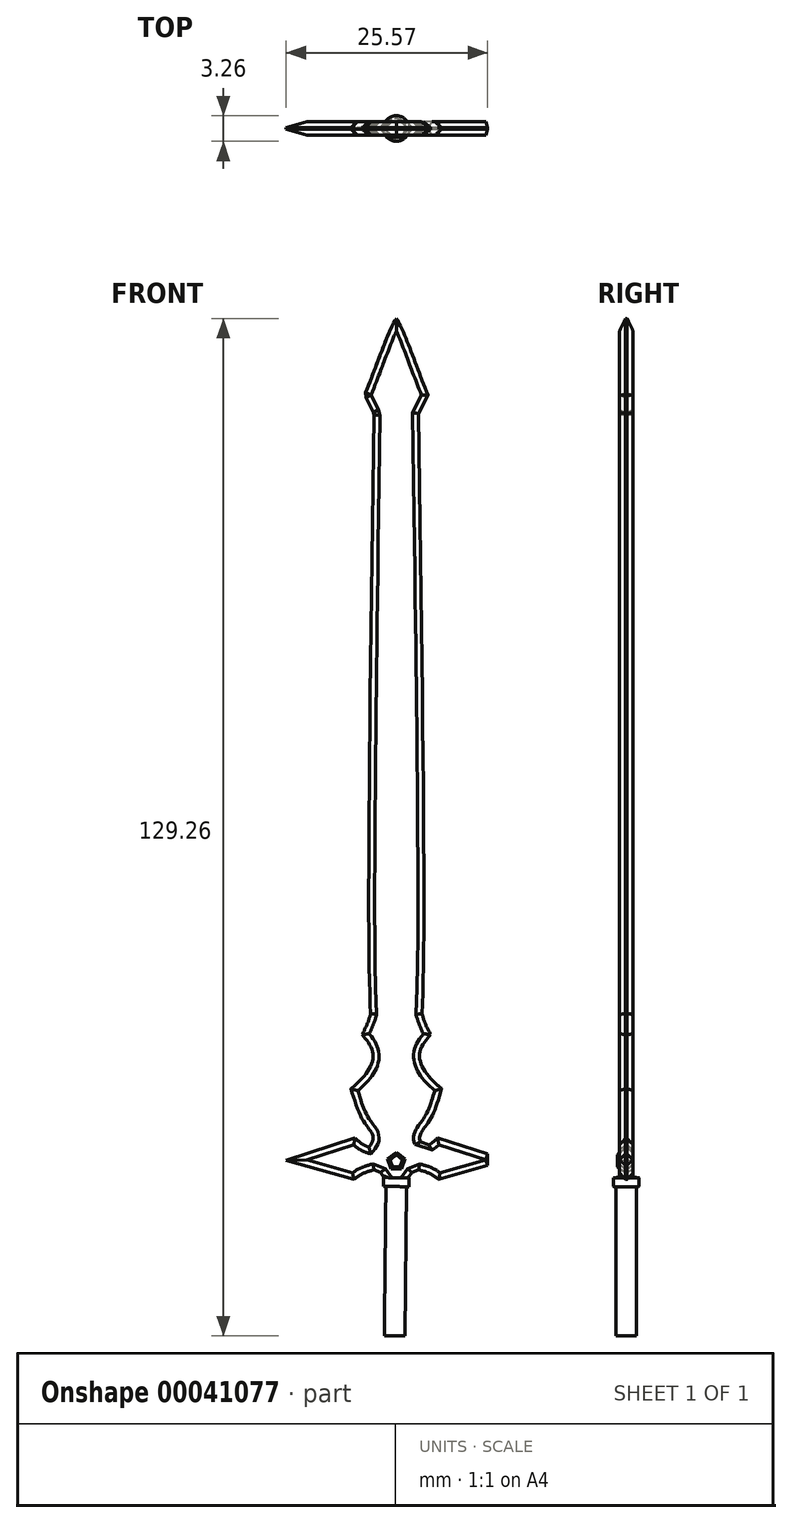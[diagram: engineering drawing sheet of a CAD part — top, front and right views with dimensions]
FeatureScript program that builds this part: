
annotation { "Feature Type Name" : "Feature", "Feature Type Description" : "" }
export const myFeature = defineFeature(function(context is Context, id is Id, definition is map)
    precondition{}
    {
        {
            var Q0;
            Q0=qCreatedBy(makeId("Front.planeOp"),FACE);
            var sketch = newSketch(context, id + "F0", { "sketchPlane" : qUnion([Q0])});
            skFitSpline(sketch, "E0", {"points": [v(5.64, -23.5) * mm, v(4.37, -24.78) * mm, v(3, -26.96) * mm, v(3.73, -29.6) * mm, v(7.73, -33.15) * mm], "startDerivative": vector(-6.28, -5.97) * mm, "endDerivative": vector(13.99, -10.4) * mm});
            skFitSpline(sketch, "E1", {"points": [v(6.28, -29.78) * mm, v(4.28, -35.6) * mm, v(3.1, -37.33) * mm, v(3.1, -38.51) * mm, v(5.19, -40.52) * mm], "startDerivative": vector(-5, -18.26) * mm, "endDerivative": vector(10.5, -8.04) * mm});
            skFitSpline(sketch, "E2", {"points": [v(6.17, -26.5) * mm, v(5.19, -25.87) * mm, v(3.46, -22.78) * mm, v(2.64, -18.05) * mm], "startDerivative": vector(-4.56, 2.08) * mm, "endDerivative": vector(-1.1, 11.4) * mm});
            skFitSpline(sketch, "E3", {"points": [v(3.1, -25.05) * mm, v(3.46, -15.5) * mm, v(2.8, 56.95) * mm], "startDerivative": vector(1.67, 27.47) * mm, "endDerivative": vector(-1.73, 121.84) * mm});
            skFitSpline(sketch, "E4", {"points": [v(1.28, 51.03) * mm, v(5.66, 59.65) * mm], "startDerivative": vector(4.37, 8.62) * mm, "endDerivative": vector(4.37, 8.62) * mm});
            skFitSpline(sketch, "E5", {"points": [v(-2.07, 68.66) * mm, v(0, 66.21) * mm, v(2.36, 60.7) * mm, v(5.42, 52.98) * mm], "startDerivative": vector(8.58, -8.47) * mm, "endDerivative": vector(7.87, -19.45) * mm});
            skFitSpline(sketch, "E6", {"points": [v(2.5, -39.2) * mm, v(3.96, -38.89) * mm, v(6, -37.16) * mm], "startDerivative": vector(3.37, 0.26) * mm, "endDerivative": vector(3.62, 3.67) * mm});
            skFitSpline(sketch, "E7", {"points": [v(4.55, -37.7) * mm, v(15.78, -41.3) * mm], "startDerivative": vector(11.23, -3.6) * mm, "endDerivative": vector(11.23, -3.6) * mm});
            skFitSpline(sketch, "E8", {"points": [v(4.69, -43.39) * mm, v(15.46, -40.3) * mm], "startDerivative": vector(10.78, 3.1) * mm, "endDerivative": vector(10.78, 3.1) * mm});
            skFitSpline(sketch, "E9", {"points": [v(6, -43.8) * mm, v(4.46, -42.53) * mm, v(1.68, -41.7) * mm], "startDerivative": vector(-3.02, 3.1) * mm, "endDerivative": vector(-5.54, 1.14) * mm});
            skFitSpline(sketch, "E10", {"points": [v(2.87, -41.07) * mm, v(0.87, -43.84) * mm], "startDerivative": vector(-2, -2.77) * mm, "endDerivative": vector(-2, -2.77) * mm});
            skFitSpline(sketch, "E11", {"points": [v(2.46, -42.98) * mm, v(-2.9, -42.92) * mm], "startDerivative": vector(-5.37, 0.06) * mm, "endDerivative": vector(-5.37, 0.06) * mm});
            skFitSpline(sketch, "E12.MirrorCS", {"points": [v(-6, -43.8) * mm, v(-4.46, -42.53) * mm, v(-1.68, -41.7) * mm], "startDerivative": vector(3.02, 3.1) * mm, "endDerivative": vector(5.54, 1.14) * mm});
            skFitSpline(sketch, "E13.MirrorCS", {"points": [v(-2.87, -41.07) * mm, v(-0.87, -43.84) * mm], "startDerivative": vector(2, -2.77) * mm, "endDerivative": vector(2, -2.77) * mm});
            skFitSpline(sketch, "E14.MirrorCS", {"points": [v(-2.5, -39.2) * mm, v(-3.96, -38.89) * mm, v(-6, -37.16) * mm], "startDerivative": vector(-3.37, 0.26) * mm, "endDerivative": vector(-3.62, 3.67) * mm});
            skFitSpline(sketch, "E15.MirrorCS", {"points": [v(-6.17, -26.5) * mm, v(-5.19, -25.87) * mm, v(-3.46, -22.78) * mm, v(-2.64, -18.05) * mm], "startDerivative": vector(4.56, 2.08) * mm, "endDerivative": vector(1.1, 11.4) * mm});
            skFitSpline(sketch, "E16.MirrorCS", {"points": [v(-5.64, -23.5) * mm, v(-4.37, -24.78) * mm, v(-3, -26.96) * mm, v(-3.73, -29.6) * mm, v(-7.73, -33.15) * mm], "startDerivative": vector(6.28, -5.97) * mm, "endDerivative": vector(-13.99, -10.4) * mm});
            skFitSpline(sketch, "E17.MirrorCS", {"points": [v(-2.46, -42.98) * mm, v(2.9, -42.92) * mm], "startDerivative": vector(5.37, 0.06) * mm, "endDerivative": vector(5.37, 0.06) * mm});
            skFitSpline(sketch, "E18.MirrorCS", {"points": [v(-4.69, -43.39) * mm, v(-15.46, -40.3) * mm], "startDerivative": vector(-10.78, 3.1) * mm, "endDerivative": vector(-10.78, 3.1) * mm});
            skFitSpline(sketch, "E19.MirrorCS", {"points": [v(-4.55, -37.7) * mm, v(-15.78, -41.3) * mm], "startDerivative": vector(-11.23, -3.6) * mm, "endDerivative": vector(-11.23, -3.6) * mm});
            skFitSpline(sketch, "E20.MirrorCS", {"points": [v(2.07, 68.66) * mm, v(0, 66.21) * mm, v(-2.36, 60.7) * mm, v(-5.42, 52.98) * mm], "startDerivative": vector(-8.58, -8.47) * mm, "endDerivative": vector(-7.87, -19.45) * mm});
            skFitSpline(sketch, "E21.MirrorCS", {"points": [v(-1.28, 51.03) * mm, v(-5.66, 59.65) * mm], "startDerivative": vector(-4.37, 8.62) * mm, "endDerivative": vector(-4.37, 8.62) * mm});
            skFitSpline(sketch, "E22.MirrorCS", {"points": [v(-6.28, -29.78) * mm, v(-4.28, -35.6) * mm, v(-3.1, -37.33) * mm, v(-3.1, -38.51) * mm, v(-5.19, -40.52) * mm], "startDerivative": vector(5, -18.26) * mm, "endDerivative": vector(-10.5, -8.04) * mm});
            skFitSpline(sketch, "E23.MirrorCS", {"points": [v(-3.1, -25.05) * mm, v(-3.46, -15.5) * mm, v(-2.8, 56.95) * mm], "startDerivative": vector(-1.67, 27.47) * mm, "endDerivative": vector(1.73, 121.84) * mm});
            skLineSegment(sketch, "E24.trimOffspring", {"start": v(1.52, -42.94) * mm, "end": v(1.52, -42.94) * mm});
            skLineSegment(sketch, "E25.trimOffspring", {"start": v(-1.52, -42.94) * mm, "end": v(-1.52, -42.94) * mm});
            skSolve(sketch);
        }
        {
            var Q0;
            Q0 = qSketchRegion(id + "F0", true);
            var Q1;
            Q1=makeQuery(id+"F0.imprint","IMPRINT",FACE,{"disambiguationData":[TD([[makeQuery(id+"F0.imprint","IMPRINT",EDGE,{"derivedFrom":sQuery(id+"F0.wireOp",EDGE,"E0")}),-1.0]])]});
            extrude(context, id + "F1", {"entities" : qUnion([Q0, Q1]), "endBound" : BoundingType.SYMMETRIC, "depth" : 1.72 * mm});
        }
        {
            var Q0;
            Q0=makeQuery(id+"F1.opExtrude","CAP_EDGE",EDGE,{"disambiguationData":[OSD([sQuery(id+"F0.wireOp",EDGE,"E5")])],"isStart":false});
            var Q1;
            Q1=makeQuery(id+"F1.opExtrude","CAP_EDGE",EDGE,{"disambiguationData":[OSD([sQuery(id+"F0.wireOp",EDGE,"E3")])],"isStart":true});
            var Q2;
            Q2=makeQuery(id+"F1.opExtrude","CAP_EDGE",EDGE,{"disambiguationData":[OSD([sQuery(id+"F0.wireOp",EDGE,"E3")])],"isStart":false});
            var Q3;
            Q3=makeQuery(id+"F1.opExtrude","CAP_EDGE",EDGE,{"disambiguationData":[OSD([sQuery(id+"F0.wireOp",EDGE,"E8")])],"isStart":false});
            var Q4;
            Q4=makeQuery(id+"F1.opExtrude","CAP_EDGE",EDGE,{"disambiguationData":[OSD([sQuery(id+"F0.wireOp",EDGE,"E0")])],"isStart":false});
            var Q5;
            Q5=makeQuery(id+"F1.opExtrude","CAP_EDGE",EDGE,{"disambiguationData":[OSD([sQuery(id+"F0.wireOp",EDGE,"E20.MirrorCS")])],"isStart":false});
            var Q6;
            Q6=makeQuery(id+"F1.opExtrude","CAP_EDGE",EDGE,{"disambiguationData":[OSD([sQuery(id+"F0.wireOp",EDGE,"E7")])],"isStart":false});
            var Q7;
            Q7=makeQuery(id+"F1.opExtrude","CAP_EDGE",EDGE,{"disambiguationData":[OSD([sQuery(id+"F0.wireOp",EDGE,"E1")])],"isStart":false});
            var Q8;
            Q8=makeQuery(id+"F1.opExtrude","CAP_EDGE",EDGE,{"disambiguationData":[OSD([sQuery(id+"F0.wireOp",EDGE,"E20.MirrorCS")])],"isStart":true});
            var Q9;
            Q9=makeQuery(id+"F1.opExtrude","CAP_EDGE",EDGE,{"disambiguationData":[OSD([sQuery(id+"F0.wireOp",EDGE,"E21.MirrorCS")])],"isStart":false});
            var Q10;
            Q10=makeQuery(id+"F1.opExtrude","CAP_EDGE",EDGE,{"disambiguationData":[OSD([sQuery(id+"F0.wireOp",EDGE,"E7")])],"isStart":true});
            var Q11;
            Q11=makeQuery(id+"F1.opExtrude","CAP_EDGE",EDGE,{"disambiguationData":[OSD([sQuery(id+"F0.wireOp",EDGE,"E5")])],"isStart":true});
            var Q12;
            Q12=makeQuery(id+"F1.opExtrude","CAP_EDGE",EDGE,{"disambiguationData":[OSD([sQuery(id+"F0.wireOp",EDGE,"E1")])],"isStart":true});
            var Q13;
            Q13=makeQuery(id+"F1.opExtrude","CAP_EDGE",EDGE,{"disambiguationData":[OSD([sQuery(id+"F0.wireOp",EDGE,"E0")])],"isStart":true});
            var Q14;
            Q14=makeQuery(id+"F1.opExtrude","CAP_EDGE",EDGE,{"disambiguationData":[OSD([sQuery(id+"F0.wireOp",EDGE,"E4")])],"isStart":false});
            var Q15;
            Q15=makeQuery(id+"F1.opExtrude","CAP_EDGE",EDGE,{"disambiguationData":[OSD([sQuery(id+"F0.wireOp",EDGE,"E6")])],"isStart":false});
            var Q16;
            Q16=makeQuery(id+"F1.opExtrude","CAP_EDGE",EDGE,{"disambiguationData":[OSD([sQuery(id+"F0.wireOp",EDGE,"E2")])],"isStart":false});
            var Q17;
            Q17=makeQuery(id+"F1.opExtrude","CAP_EDGE",EDGE,{"disambiguationData":[OSD([sQuery(id+"F0.wireOp",EDGE,"E9")])],"isStart":false});
            var Q18;
            Q18=makeQuery(id+"F1.opExtrude","CAP_EDGE",EDGE,{"disambiguationData":[OSD([sQuery(id+"F0.wireOp",EDGE,"E6")])],"isStart":true});
            var Q19;
            Q19=makeQuery(id+"F1.opExtrude","CAP_EDGE",EDGE,{"disambiguationData":[OSD([sQuery(id+"F0.wireOp",EDGE,"E2")])],"isStart":true});
            var Q20;
            Q20=makeQuery(id+"F1.opExtrude","CAP_EDGE",EDGE,{"disambiguationData":[OSD([sQuery(id+"F0.wireOp",EDGE,"E9")])],"isStart":true});
            var Q21;
            Q21=makeQuery(id+"F1.opExtrude","CAP_EDGE",EDGE,{"disambiguationData":[OSD([sQuery(id+"F0.wireOp",EDGE,"E8")])],"isStart":true});
            var Q22;
            Q22=makeQuery(id+"F1.opExtrude","SWEPT_EDGE",EDGE,{"disambiguationData":[OSD([sQuery(id+"F0.wireOp",EDGE,"E7"),sQuery(id+"F0.wireOp",EDGE,"E8")])]});
            var Q23;
            Q23=makeQuery(id+"F1.opExtrude","CAP_EDGE",EDGE,{"disambiguationData":[OSD([sQuery(id+"F0.wireOp",EDGE,"E21.MirrorCS")])],"isStart":true});
            var Q24;
            Q24=makeQuery(id+"F1.opExtrude","CAP_EDGE",EDGE,{"disambiguationData":[OSD([sQuery(id+"F0.wireOp",EDGE,"E4")])],"isStart":true});
            var Q25;
            Q25=makeQuery(id+"F1.opExtrude","SWEPT_EDGE",EDGE,{"disambiguationData":[OSD([sQuery(id+"F0.wireOp",EDGE,"E20.MirrorCS"),sQuery(id+"F0.wireOp",EDGE,"E21.MirrorCS")])]});
            var Q26;
            Q26=makeQuery(id+"F1.opExtrude","SWEPT_EDGE",EDGE,{"disambiguationData":[OSD([sQuery(id+"F0.wireOp",EDGE,"E21.MirrorCS"),sQuery(id+"F0.wireOp",EDGE,"E23.MirrorCS")])]});
            var Q27;
            Q27=makeQuery(id+"F1.opExtrude","CAP_EDGE",EDGE,{"disambiguationData":[OSD([sQuery(id+"F0.wireOp",EDGE,"E22.MirrorCS")])],"isStart":false});
            var Q28;
            Q28=makeQuery(id+"F1.opExtrude","CAP_EDGE",EDGE,{"disambiguationData":[OSD([sQuery(id+"F0.wireOp",EDGE,"E18.MirrorCS")])],"isStart":false});
            var Q29;
            Q29=makeQuery(id+"F1.opExtrude","CAP_EDGE",EDGE,{"disambiguationData":[OSD([sQuery(id+"F0.wireOp",EDGE,"E19.MirrorCS")])],"isStart":false});
            var Q30;
            Q30=makeQuery(id+"F1.opExtrude","CAP_EDGE",EDGE,{"disambiguationData":[OSD([sQuery(id+"F0.wireOp",EDGE,"E16.MirrorCS")])],"isStart":false});
            var Q31;
            Q31=makeQuery(id+"F1.opExtrude","CAP_EDGE",EDGE,{"disambiguationData":[OSD([sQuery(id+"F0.wireOp",EDGE,"E12.MirrorCS")])],"isStart":false});
            var Q32;
            Q32=makeQuery(id+"F1.opExtrude","CAP_EDGE",EDGE,{"disambiguationData":[OSD([sQuery(id+"F0.wireOp",EDGE,"E14.MirrorCS")])],"isStart":false});
            var Q33;
            Q33=makeQuery(id+"F1.opExtrude","CAP_EDGE",EDGE,{"disambiguationData":[OSD([sQuery(id+"F0.wireOp",EDGE,"E15.MirrorCS")])],"isStart":false});
            var Q34;
            Q34=makeQuery(id+"F1.opExtrude","CAP_EDGE",EDGE,{"disambiguationData":[OSD([sQuery(id+"F0.wireOp",EDGE,"E23.MirrorCS")])],"isStart":false});
            var Q35;
            Q35=makeQuery(id+"F1.opExtrude","CAP_EDGE",EDGE,{"disambiguationData":[OSD([sQuery(id+"F0.wireOp",EDGE,"E15.MirrorCS")])],"isStart":true});
            var Q36;
            Q36=makeQuery(id+"F1.opExtrude","CAP_EDGE",EDGE,{"disambiguationData":[OSD([sQuery(id+"F0.wireOp",EDGE,"E23.MirrorCS")])],"isStart":true});
            var Q37;
            Q37=makeQuery(id+"F1.opExtrude","CAP_EDGE",EDGE,{"disambiguationData":[OSD([sQuery(id+"F0.wireOp",EDGE,"E14.MirrorCS")])],"isStart":true});
            var Q38;
            Q38=makeQuery(id+"F1.opExtrude","CAP_EDGE",EDGE,{"disambiguationData":[OSD([sQuery(id+"F0.wireOp",EDGE,"E22.MirrorCS")])],"isStart":true});
            var Q39;
            Q39=makeQuery(id+"F1.opExtrude","CAP_EDGE",EDGE,{"disambiguationData":[OSD([sQuery(id+"F0.wireOp",EDGE,"E12.MirrorCS")])],"isStart":true});
            var Q40;
            Q40=makeQuery(id+"F1.opExtrude","CAP_EDGE",EDGE,{"disambiguationData":[OSD([sQuery(id+"F0.wireOp",EDGE,"E18.MirrorCS")])],"isStart":true});
            var Q41;
            Q41=makeQuery(id+"F1.opExtrude","CAP_EDGE",EDGE,{"disambiguationData":[OSD([sQuery(id+"F0.wireOp",EDGE,"E16.MirrorCS")])],"isStart":true});
            var Q42;
            Q42=makeQuery(id+"F1.opExtrude","CAP_EDGE",EDGE,{"disambiguationData":[OSD([sQuery(id+"F0.wireOp",EDGE,"E19.MirrorCS")])],"isStart":true});
            var Q43;
            Q43=makeQuery(id+"F1.opExtrude","SWEPT_EDGE",EDGE,{"disambiguationData":[OSD([sQuery(id+"F0.wireOp",EDGE,"E1"),sQuery(id+"F0.wireOp",EDGE,"E6")])]});
            var Q44;
            Q44=makeQuery(id+"F1.opExtrude","SWEPT_EDGE",EDGE,{"disambiguationData":[OSD([sQuery(id+"F0.wireOp",EDGE,"E9"),sQuery(id+"F0.wireOp",EDGE,"E10")])]});
            var Q45;
            Q45=makeQuery(id+"F1.opExtrude","SWEPT_EDGE",EDGE,{"disambiguationData":[OSD([sQuery(id+"F0.wireOp",EDGE,"E12.MirrorCS"),sQuery(id+"F0.wireOp",EDGE,"E13.MirrorCS")])]});
            var Q46;
            Q46=makeQuery(id+"F1.opExtrude","SWEPT_FACE",FACE,{"disambiguationData":[OSD([sQuery(id+"F0.wireOp",EDGE,"E13.MirrorCS")])]});
            chamfer(context, id + "F2", {"entities" : qUnion([Q0, Q1, Q2, Q3, Q4, Q5, Q6, Q7, Q8, Q9, Q10, Q11, Q12, Q13, Q14, Q15, Q16, Q17, Q18, Q19, Q20, Q21, Q22, Q23, Q24, Q25, Q26, Q27, Q28, Q29, Q30, Q31, Q32, Q33, Q34, Q35, Q36, Q37, Q38, Q39, Q40, Q41, Q42, Q43, Q44, Q45, Q46]), "width" : 0.76 * mm, "tangentPropagation" : true});
        }
        {
            var Q0;
            Q0=makeQuery(id+"F1.opExtrude","SWEPT_FACE",FACE,{"disambiguationData":[OSD([sQuery(id+"F0.wireOp",EDGE,"E11")])]});
            var sketch = newSketch(context, id + "F3", { "sketchPlane" : qUnion([Q0])});
            skCircle(sketch, "E26", {"center": v(0.49, 0) * mm, "radius": 1.63 * mm});
            skSolve(sketch);
        }
        {
            var Q0;
            {var subQ0=sQuery(id+"F0.wireOp",EDGE,"E11");Q0=makeQuery(id+"F3.imprint","IMPRINT",FACE,{"disambiguationData":[TD([[makeQuery(id+"F3.imprint","IMPRINT",EDGE,{"derivedFrom":makeQuery(id+"F1.opExtrude","CAP_EDGE",EDGE,{"disambiguationData":[OSD([subQ0])],"isStart":true})}),-1.0]])]});}
            var Q1;
            Q1=makeQuery(id+"F3.imprint","IMPRINT",FACE,{"disambiguationData":[TD([[makeQuery(id+"F3.imprint","IMPRINT",EDGE,{"derivedFrom":sQuery(id+"F3.wireOp",EDGE,"E26")}),1.0]])]});
            extrude(context, id + "F4", {"entities" : qUnion([Q0, Q1]), "operationType" : NewBodyOperationType.ADD, "depth" : 1.13 * mm});
        }
        {
            var Q0;
            Q0=makeQuery(id+"F4.opExtrude","CAP_FACE",FACE,{"disambiguationData":[OSD([sQuery(id+"F3.wireOp",EDGE,"E26")])],"isStart":false});
            var sketch = newSketch(context, id + "F5", { "sketchPlane" : qUnion([Q0])});
            skCircle(sketch, "E27", {"center": v(0.49, 0) * mm, "radius": 1.3 * mm});
            skSolve(sketch);
        }
        {
            var Q0;
            Q0=makeQuery(id+"F5.imprint","IMPRINT",FACE,{"disambiguationData":[TD([[makeQuery(id+"F5.imprint","IMPRINT",EDGE,{"derivedFrom":sQuery(id+"F5.wireOp",EDGE,"E27")}),1.0]])]});
            extrude(context, id + "F6", {"entities" : qUnion([Q0]), "operationType" : NewBodyOperationType.ADD, "depth" : 18.96 * mm});
        }
        {
            var Q0;
            Q0=makeQuery(id+"F1.opExtrude","CAP_FACE",FACE,{"disambiguationData":[OSD([sQuery(id+"F0.wireOp",EDGE,"E0"),sQuery(id+"F0.wireOp",EDGE,"E1"),sQuery(id+"F0.wireOp",EDGE,"E2"),sQuery(id+"F0.wireOp",EDGE,"E3"),sQuery(id+"F0.wireOp",EDGE,"E4"),sQuery(id+"F0.wireOp",EDGE,"E5"),sQuery(id+"F0.wireOp",EDGE,"E6"),sQuery(id+"F0.wireOp",EDGE,"E7"),sQuery(id+"F0.wireOp",EDGE,"E8"),sQuery(id+"F0.wireOp",EDGE,"E9"),sQuery(id+"F0.wireOp",EDGE,"E10"),sQuery(id+"F0.wireOp",EDGE,"E11"),sQuery(id+"F0.wireOp",EDGE,"E12.MirrorCS"),sQuery(id+"F0.wireOp",EDGE,"E13.MirrorCS"),sQuery(id+"F0.wireOp",EDGE,"E14.MirrorCS"),sQuery(id+"F0.wireOp",EDGE,"E15.MirrorCS"),sQuery(id+"F0.wireOp",EDGE,"E16.MirrorCS"),sQuery(id+"F0.wireOp",EDGE,"E17.MirrorCS"),sQuery(id+"F0.wireOp",EDGE,"E18.MirrorCS"),sQuery(id+"F0.wireOp",EDGE,"E19.MirrorCS"),sQuery(id+"F0.wireOp",EDGE,"E20.MirrorCS"),sQuery(id+"F0.wireOp",EDGE,"E21.MirrorCS"),sQuery(id+"F0.wireOp",EDGE,"E22.MirrorCS"),sQuery(id+"F0.wireOp",EDGE,"E23.MirrorCS")])],"isStart":false});
            var sketch = newSketch(context, id + "F7", { "sketchPlane" : qUnion([Q0])});
            skCircle(sketch, "E28.cCircle", {"center": v(0, -40.92) * mm, "radius": 0.93 * mm, "construction": true});
            skLineSegment(sketch, "E28.0", {"start": v(0.68, -41.85) * mm, "end": v(-0.68, -41.85) * mm});
            skLineSegment(sketch, "E28.1", {"start": v(-0.68, -41.85) * mm, "end": v(-1.1, -40.56) * mm});
            skLineSegment(sketch, "E28.2", {"start": v(-1.1, -40.56) * mm, "end": v(0, -39.76) * mm});
            skLineSegment(sketch, "E28.3", {"start": v(0, -39.76) * mm, "end": v(1.1, -40.56) * mm});
            skLineSegment(sketch, "E28.4", {"start": v(1.1, -40.56) * mm, "end": v(0.68, -41.85) * mm});
            skPoint(sketch, "E28.0.midPoint", {"position": v(0, -41.85) * mm});
            skSolve(sketch);
        }
        {
            var Q0;
            Q0=makeQuery(id+"F7.imprint","IMPRINT",FACE,{"disambiguationData":[TD([[makeQuery(id+"F7.imprint","IMPRINT",EDGE,{"derivedFrom":sQuery(id+"F7.wireOp",EDGE,"E28.0")}),-1.0]])]});
            extrude(context, id + "F8", {"entities" : qUnion([Q0]), "operationType" : NewBodyOperationType.ADD, "depth" : 0.27 * mm});
        }
        {
            var Q0;
            Q0=makeQuery(id+"F8.opExtrude","CAP_EDGE",EDGE,{"disambiguationData":[OSD([sQuery(id+"F7.wireOp",EDGE,"E28.4")])],"isStart":false});
            var Q1;
            Q1=makeQuery(id+"F8.opExtrude","CAP_EDGE",EDGE,{"disambiguationData":[OSD([sQuery(id+"F7.wireOp",EDGE,"E28.3")])],"isStart":false});
            var Q2;
            Q2=makeQuery(id+"F8.opExtrude","CAP_EDGE",EDGE,{"disambiguationData":[OSD([sQuery(id+"F7.wireOp",EDGE,"E28.2")])],"isStart":false});
            var Q3;
            Q3=makeQuery(id+"F8.opExtrude","CAP_EDGE",EDGE,{"disambiguationData":[OSD([sQuery(id+"F7.wireOp",EDGE,"E28.1")])],"isStart":false});
            var Q4;
            Q4=makeQuery(id+"F8.opExtrude","CAP_EDGE",EDGE,{"disambiguationData":[OSD([sQuery(id+"F7.wireOp",EDGE,"E28.0")])],"isStart":false});
            chamfer(context, id + "F9", {"entities" : qUnion([Q0, Q1, Q2, Q3, Q4]), "width" : 0.25 * mm, "tangentPropagation" : true});
        }
    });
